# Revit family: TMI - W1050 - Wall_Open1
name_source: partatom
category: Casework
revit_build: Autodesk Revit 2016 (Build: 20150220_1215(x64)
units: mm (PartAtom-declared; Revit-internal decimal feet)

## family parameters
Cut with Voids When Loaded = No
Host = Face
OmniClass Number = 23.40.35.14.11
OmniClass Title = Modular Casework
Room Calculation Point = No
Shared = No

## types (9) — shared parameters
Cabinet Finish = Plastic Laminate
Casework Back Thickness = 1/4"
Casework Thickness = 3/4"
Default Elevation = 84"
Depth = 13"
Description = Wall, Open, Adj. Shelf
Height = 30"
Interior Finish = <By Category>
Manufacturer = TMI Systems Corporation
Model = W1050
Shelf Thickness = 3/4"
TFM Thickness = 1/32"
URL = www.tmisystems.com

## per-type parameters (varying)
| type | Width |
| 24" x 30" x 13" | 24" |
| 27" x 30" x 13" | 27" |
| 30" x 30" x 13" | 30" |
| 33" x 30" x 13" | 33" |
| 36" x 30" x 13" | 36" |
| 21" x 30" x 13" | 21" |
| 18" x 30" x 13" | 18" |
| 15" x 30" x 13" | 15" |
| 12" x 30" x 13" | 12" |

## geometry (parser evidence)
native form markers: Blend x2, Sweep x3
no freeform markers — native parametric forms only
